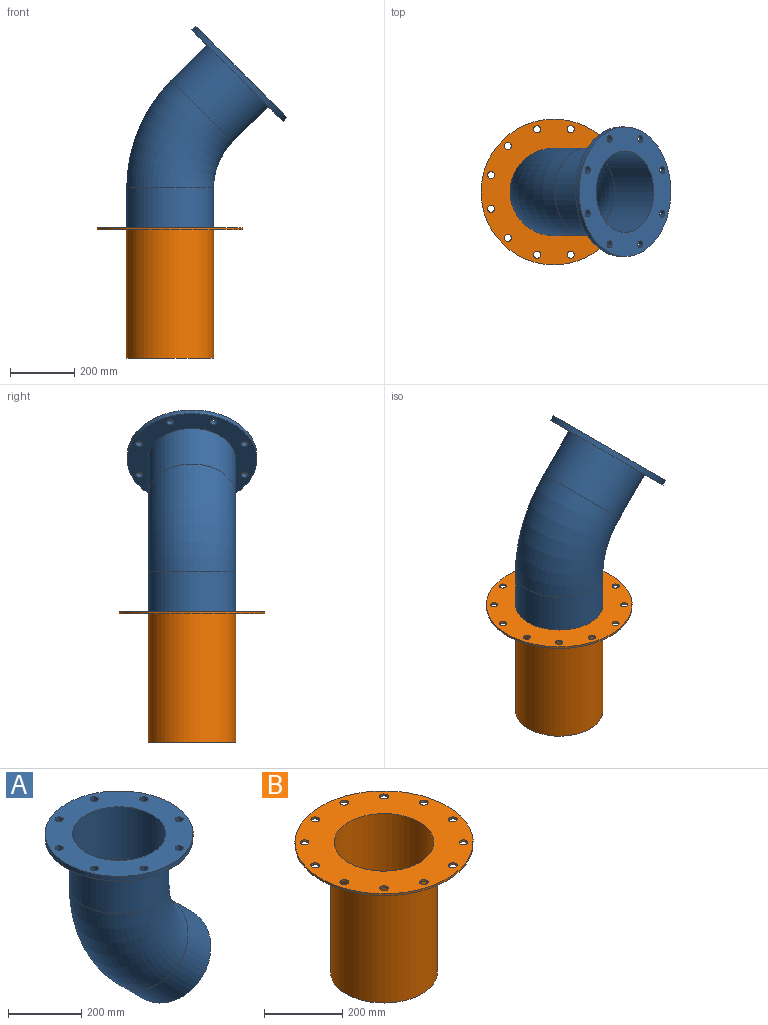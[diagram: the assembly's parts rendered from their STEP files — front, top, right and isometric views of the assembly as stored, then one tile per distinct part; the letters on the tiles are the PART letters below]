
ASSEMBLY  parts=2 mates=1
PART A: 18 faces, bbox 487x405x598.3 mm
  f0: cylinder r=127.23mm len=254.46mm, axis (0,0,1), area 138297.9mm2, adj f4,f5
  f1: cylinder r=136.5mm len=273mm, axis (0,0,1), area 134651.8mm2, adj f2,f6
  f2: plane 405x405mm, normal (0,0,-1), area 67248.9mm2, adj f1,f3,f10,f11,f12,f13,f14,f15
  f3: cylinder r=202.5mm len=405mm, axis (0,0,1), area 20357.5mm2, adj f2,f4
  f4: plane 405x405mm, normal (0,0,1), area 74929.4mm2, adj f0,f3,f10,f11,f12,f13,f14,f15
  f5: torus R=340mm, axis (0,-1,0), area 213470.7mm2, adj f0,f8
  f6: torus R=340mm, axis (0,-1,0), area 229024.2mm2, adj f1,f7
  f7: cylinder r=136.5mm len=281.43mm, axis (-0.71,0,0.71), area 107206.8mm2, adj f6,f9
  f8: cylinder r=127.23mm len=268.32mm, axis (-0.71,0,0.71), area 99926.2mm2, adj f5,f9
  f9: plane 273x193.04mm, normal (0.71,0,-0.71), area 7680.5mm2, adj f7,f8
  f10: cylinder r=11mm len=22mm, axis (0,0,1), area 1105.8mm2, adj f2,f4
  f11: cylinder r=11mm len=22mm, axis (0,0,1), area 1105.8mm2, adj f2,f4
  f12: cylinder r=11mm len=22mm, axis (0,0,1), area 1105.8mm2, adj f2,f4
  f13: cylinder r=11mm len=22mm, axis (0,0,1), area 1105.8mm2, adj f2,f4
  f14: cylinder r=11mm len=22mm, axis (0,0,1), area 1105.8mm2, adj f2,f4
  f15: cylinder r=11mm len=22mm, axis (0,0,1), area 1105.8mm2, adj f2,f4
  f16: cylinder r=11mm len=22mm, axis (0,0,1), area 1105.8mm2, adj f2,f4
  f17: cylinder r=11mm len=22mm, axis (0,0,1), area 1105.8mm2, adj f2,f4
PART B: 18 faces, bbox 455x455x406 mm
  f0: cylinder r=11mm len=22mm, axis (0,0,-1), area 414.7mm2, adj f13,f14
  f1: cylinder r=11mm len=22mm, axis (0,0,-1), area 414.7mm2, adj f13,f14
  f2: cylinder r=11mm len=22mm, axis (0,0,-1), area 414.7mm2, adj f13,f14
  f3: cylinder r=11mm len=22mm, axis (0,0,-1), area 414.7mm2, adj f13,f14
  f4: cylinder r=11mm len=22mm, axis (0,0,-1), area 414.7mm2, adj f13,f14
  f5: cylinder r=11mm len=22mm, axis (0,0,-1), area 414.7mm2, adj f13,f14
  f6: cylinder r=11mm len=22mm, axis (0,0,-1), area 414.7mm2, adj f13,f14
  f7: cylinder r=11mm len=22mm, axis (0,0,-1), area 414.7mm2, adj f13,f14
  f8: cylinder r=11mm len=22mm, axis (0,0,-1), area 414.7mm2, adj f13,f14
  f9: cylinder r=11mm len=22mm, axis (0,0,-1), area 414.7mm2, adj f13,f14
  f10: cylinder r=11mm len=22mm, axis (0,0,-1), area 414.7mm2, adj f13,f14
  f11: cylinder r=11mm len=22mm, axis (0,0,-1), area 414.7mm2, adj f13,f14
  f12: cylinder r=227.5mm len=455mm, axis (0,0,-1), area 8576.5mm2, adj f13,f14
  f13: plane 455x455mm, normal (0,0,1), area 107181mm2, adj f0,f1,f2,f3,f4,f5,f6,f7
  f14: plane 455x455mm, normal (0,0,-1), area 99500.5mm2, adj f0,f1,f2,f3,f4,f5,f6,f7
  f15: cylinder r=136.5mm len=400mm, axis (0,0,1), area 343061.9mm2, adj f14,f17
  f16: cylinder r=127.23mm len=406mm, axis (0,0,1), area 324560.3mm2, adj f13,f17
  f17: plane 273x273mm, normal (0,0,-1), area 7680.5mm2, adj f15,f16
PLACE A rot(axis=(0,1,0),45deg) t=(755.02,-150.33,-346.72)mm
PLACE B t=(-670.74,182.67,-1153.62)mm
MATE fastened A.f7 <-> B.f12  axis (0,0,-1) through (-670.74,-150.33,369.38)mm
